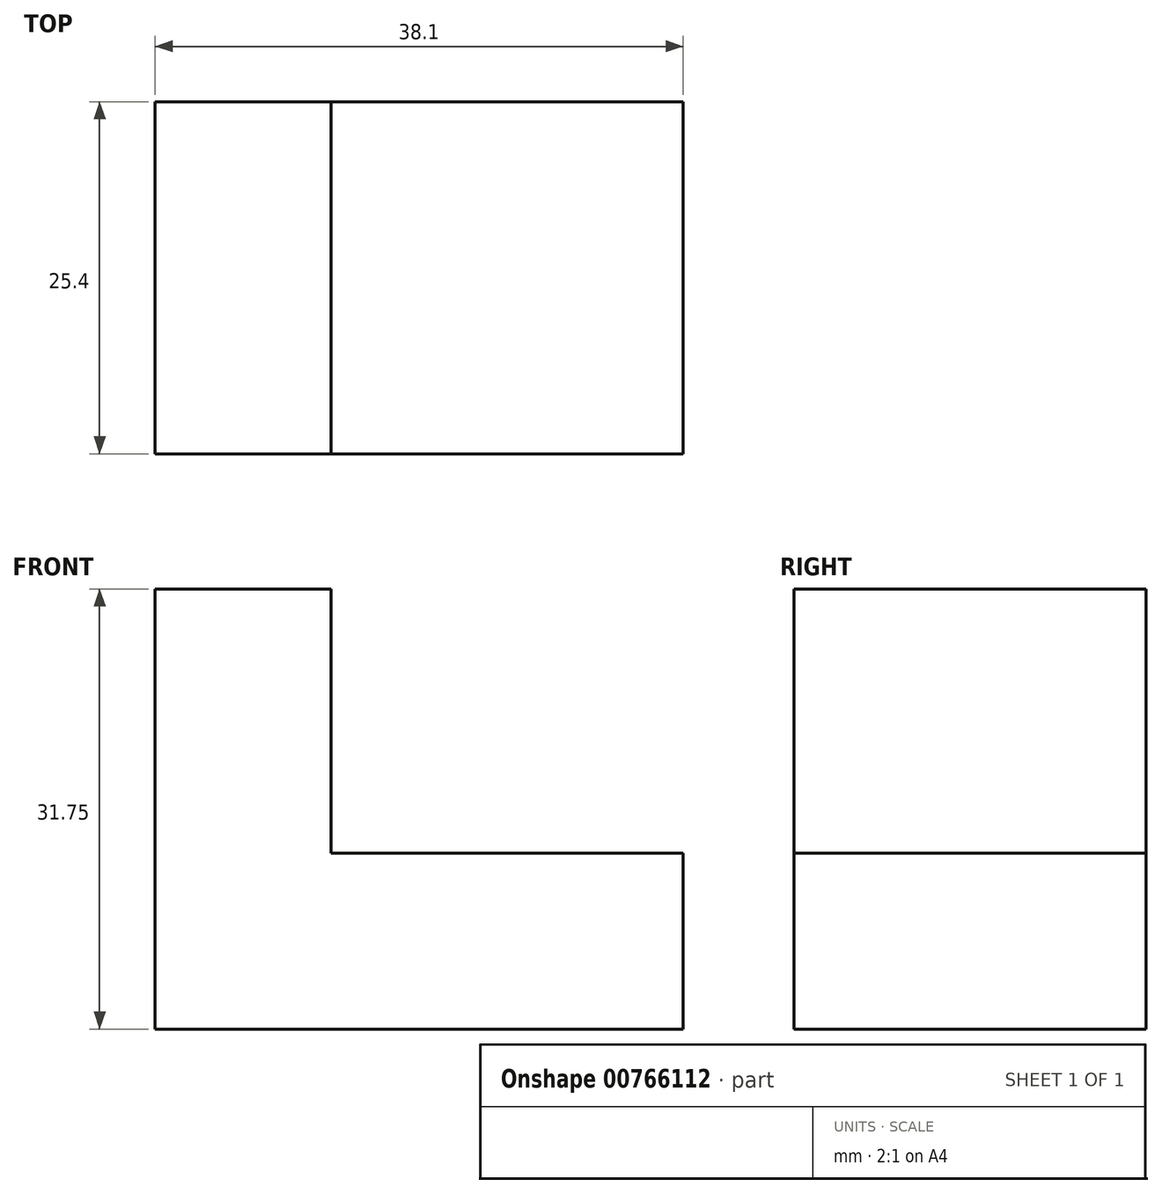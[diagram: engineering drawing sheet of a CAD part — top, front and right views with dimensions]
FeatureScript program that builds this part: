
annotation { "Feature Type Name" : "Feature", "Feature Type Description" : "" }
export const myFeature = defineFeature(function(context is Context, id is Id, definition is map)
    precondition{}
    {
        {
            var Q0;
            Q0=qCreatedBy(makeId("Front.planeOp"),FACE);
            var sketch = newSketch(context, id + "F0", { "sketchPlane" : qUnion([Q0])});
            skLineSegment(sketch, "E0", {"start": v(0, 0) * mm, "end": v(38.1, 0) * mm});
            skLineSegment(sketch, "E1", {"start": v(38.1, 0) * mm, "end": v(38.1, 0) * mm});
            skLineSegment(sketch, "E2", {"start": v(38.1, 0) * mm, "end": v(38.1, 12.7) * mm});
            skLineSegment(sketch, "E3", {"start": v(38.1, 12.7) * mm, "end": v(12.7, 12.7) * mm});
            skLineSegment(sketch, "E4", {"start": v(12.7, 12.7) * mm, "end": v(12.7, 31.75) * mm});
            skLineSegment(sketch, "E5", {"start": v(12.7, 31.75) * mm, "end": v(0, 31.75) * mm});
            skLineSegment(sketch, "E6", {"start": v(0, 31.75) * mm, "end": v(0, 0) * mm});
            skSolve(sketch);
        }
        {
            var Q0;
            Q0 = qSketchRegion(id + "F0", true);
            extrude(context, id + "F1", {"entities" : qUnion([Q0]), "depth" : 25.4 * mm, "offsetDistance" : 25.4 * mm});
        }
    });
